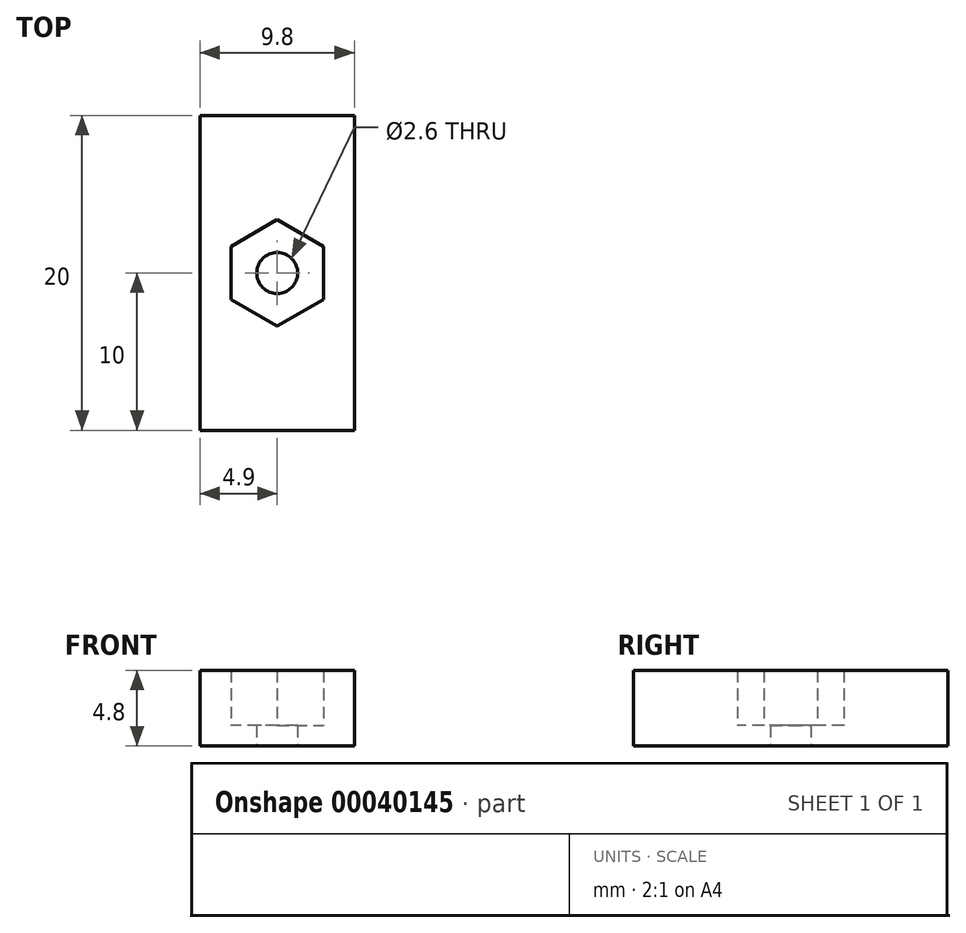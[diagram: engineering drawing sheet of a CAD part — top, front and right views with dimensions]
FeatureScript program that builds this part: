
annotation { "Feature Type Name" : "Feature", "Feature Type Description" : "" }
export const myFeature = defineFeature(function(context is Context, id is Id, definition is map)
    precondition{}
    {
        {
            var Q0;
            Q0=qCreatedBy(makeId("Top.planeOp"),FACE);
            var sketch = newSketch(context, id + "F0", { "sketchPlane" : qUnion([Q0])});
            skLineSegment(sketch, "E0.rect.bottom", {"start": v(4.9, -10) * mm, "end": v(-4.9, -10) * mm});
            skLineSegment(sketch, "E0.rect.top", {"start": v(4.9, 10) * mm, "end": v(-4.9, 10) * mm});
            skLineSegment(sketch, "E0.rect.left", {"start": v(4.9, -10) * mm, "end": v(4.9, 10) * mm});
            skLineSegment(sketch, "E0.rect.right", {"start": v(-4.9, -10) * mm, "end": v(-4.9, 10) * mm});
            skCircle(sketch, "E1.cCircle", {"center": v(0, 0) * mm, "radius": 2.93 * mm, "construction": true});
            skLineSegment(sketch, "E1.0", {"start": v(2.93, 1.69) * mm, "end": v(2.93, -1.69) * mm});
            skLineSegment(sketch, "E1.1", {"start": v(2.92, -1.69) * mm, "end": v(0, -3.38) * mm});
            skLineSegment(sketch, "E1.2", {"start": v(0, -3.38) * mm, "end": v(-2.93, -1.69) * mm});
            skLineSegment(sketch, "E1.3", {"start": v(-2.93, -1.69) * mm, "end": v(-2.93, 1.69) * mm});
            skLineSegment(sketch, "E1.4", {"start": v(-2.93, 1.69) * mm, "end": v(0, 3.38) * mm});
            skLineSegment(sketch, "E1.5", {"start": v(0, 3.38) * mm, "end": v(2.93, 1.69) * mm});
            skPoint(sketch, "E1.0.midPoint", {"position": v(2.93, 0) * mm});
            skCircle(sketch, "E2", {"center": v(0, 0) * mm, "radius": 1.3 * mm});
            skSolve(sketch);
        }
        {
            var Q0;
            Q0=makeQuery(id+"F0.imprint","IMPRINT",FACE,{"disambiguationData":[TD([[makeQuery(id+"F0.imprint","IMPRINT",EDGE,{"derivedFrom":sQuery(id+"F0.wireOp",EDGE,"E0.rect.bottom")}),-1.0]])]});
            extrude(context, id + "F1", {"entities" : qUnion([Q0]), "depth" : 4.8 * mm});
        }
        {
            var Q0;
            Q0=makeQuery(id+"F0.imprint","IMPRINT",FACE,{"disambiguationData":[TD([[makeQuery(id+"F0.imprint","IMPRINT",EDGE,{"derivedFrom":sQuery(id+"F0.wireOp",EDGE,"E1.0")}),-1.0]])]});
            extrude(context, id + "F2", {"entities" : qUnion([Q0]), "operationType" : NewBodyOperationType.ADD, "depth" : 1.3 * mm});
        }
    });
